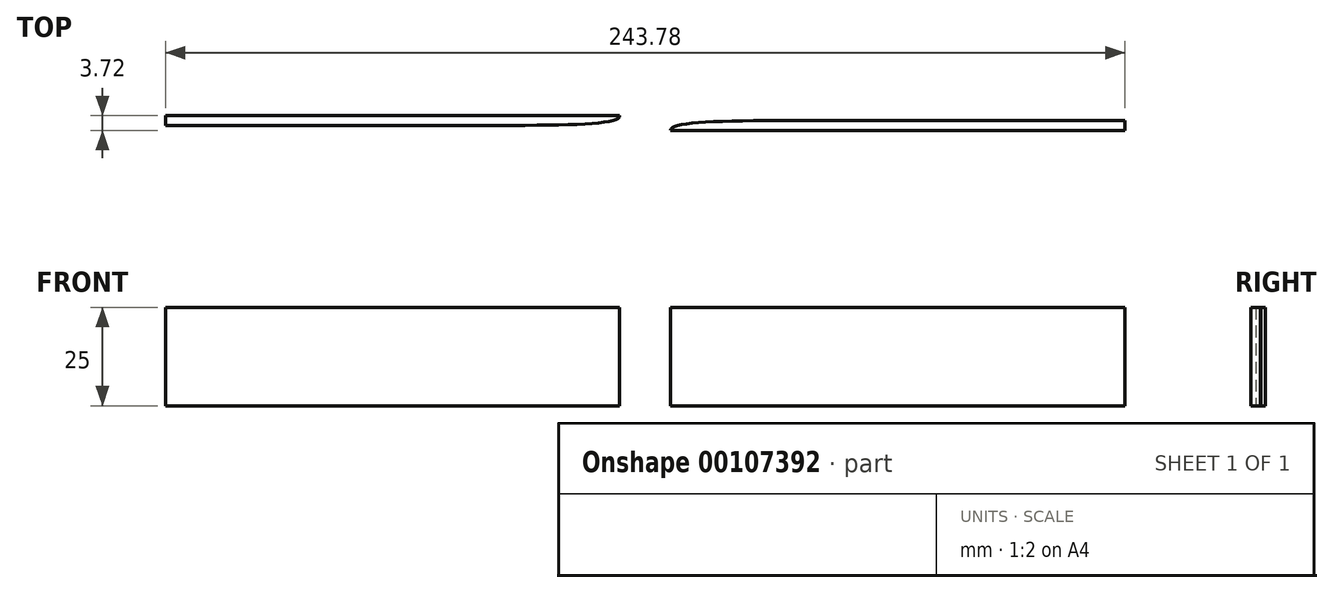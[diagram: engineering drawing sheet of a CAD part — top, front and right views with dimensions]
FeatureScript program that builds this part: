
annotation { "Feature Type Name" : "Feature", "Feature Type Description" : "" }
export const myFeature = defineFeature(function(context is Context, id is Id, definition is map)
    precondition{}
    {
        {
            var Q0;
            Q0=qCreatedBy(makeId("Top.planeOp"),FACE);
            var sketch = newSketch(context, id + "F0", { "sketchPlane" : qUnion([Q0])});
            skLineSegment(sketch, "E0.bottom", {"start": v(-121.9, 1.86) * mm, "end": v(-6.48, 1.86) * mm});
            skLineSegment(sketch, "E0.left", {"start": v(-121.9, 1.86) * mm, "end": v(-121.9, -0.6) * mm});
            skFitSpline(sketch, "E1", {"points": [v(-60.77, -0.6) * mm, v(-6.48, 1.86) * mm], "startDerivative": vector(102.2, 0) * mm, "endDerivative": vector(-0.38, 8.75) * mm});
            skLineSegment(sketch, "E2", {"start": v(-121.9, -0.6) * mm, "end": v(-60.77, -0.6) * mm});
            skSolve(sketch);
        }
        {
            var Q0;
            Q0 = qSketchRegion(id + "F0", true);
            extrude(context, id + "F1", {"entities" : qUnion([Q0]), "endBound" : BoundingType.SYMMETRIC, "depth" : 25 * mm});
        }
        {
            var Q0;
            Q0=makeQuery(id+"F1.opExtrude","SWEPT_BODY",BODY,{"disambiguationData":[OSD([sQuery(id+"F0.wireOp",EDGE,"E0.bottom"),sQuery(id+"F0.wireOp",EDGE,"E0.left"),sQuery(id+"F0.wireOp",EDGE,"E1"),sQuery(id+"F0.wireOp",EDGE,"E2")])]});
            var Q1;
            Q1=qCreatedBy(makeId("Right.planeOp"),FACE);
            mirror(context, id + "F2", {"entities" : qUnion([Q0]), "mirrorPlane" : qUnion([Q1])});
        }
        {
            var Q0;
            Q0=makeQuery(id+"F2.opPattern","COPY",BODY,{"derivedFrom":makeQuery(id+"F1.opExtrude","SWEPT_BODY",BODY,{"disambiguationData":[OSD([sQuery(id+"F0.wireOp",EDGE,"E0.bottom"),sQuery(id+"F0.wireOp",EDGE,"E0.left"),sQuery(id+"F0.wireOp",EDGE,"E1"),sQuery(id+"F0.wireOp",EDGE,"E2")])]}),"instanceName":"1"});
            var Q1;
            Q1=qCreatedBy(makeId("Front.planeOp"),FACE);
            mirror(context, id + "F3", {"entities" : qUnion([Q0]), "mirrorPlane" : qUnion([Q1])});
        }
        {
            var Q0;
            Q0=makeQuery(id+"F2.opPattern","COPY",BODY,{"derivedFrom":makeQuery(id+"F1.opExtrude","SWEPT_BODY",BODY,{"disambiguationData":[OSD([sQuery(id+"F0.wireOp",EDGE,"E0.bottom"),sQuery(id+"F0.wireOp",EDGE,"E0.left"),sQuery(id+"F0.wireOp",EDGE,"E1"),sQuery(id+"F0.wireOp",EDGE,"E2")])]}),"instanceName":"1"});
            deleteBodies(context, id + "F4", {"entities" : qUnion([Q0])});
        }
    });
